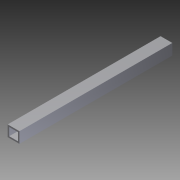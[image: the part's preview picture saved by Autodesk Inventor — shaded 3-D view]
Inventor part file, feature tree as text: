
AUTODESK INVENTOR PART (.ipt)
format: ipt  version: 2012 (Build 160160000, 160)  size: 75,776 bytes
history: native  units: in
note: dims shown in document units (in); Inventor stores cm internally (conversion verified against a paired STEP export)
features: extrude x1, sketch x1
ambient origin geometry x8: Origin, YZ Plane, XZ Plane, XY Plane, X Axis, Y Axis, Z Axis, Center Point
bodies: Solid1 (feature_tree)
feature tree (2):
  extrude  "Extrusion1"  Depth=0.9313in
  sketch  "Sketch1"  dims[d0=1.0in d1=0.9313in d2=0.125in d3=0.125in d4=0.125in d5=0.125in d6=13.0in d7=0.0in]
